# Revit family: TRP2
name_source: partatom
category: Lighting Fixtures
revit_build: Autodesk Revit 2014 (Build: 20130308_1515(x64)
units: mm (PartAtom-declared; Revit-internal decimal feet)

## types (1)
- TRP2
    Color Filter = 16777215
    Default Elevation = 48"
    Description = Mid sized architectural wallpacks in three stylish shapes with molded contours to accentuate building architecture. Provides excellent illumination in energy-saving LED systems.
    Dimming Lamp Color Temperature Shift = <None>
    Finish = Paint - Hubbell - Textured Camera Black
    Finish2 = White
    Lamp = One
    Manufacturer = Hubbell Lighting
    Model = TRP2
    Opal lens = Glass - Hubbell - White
    Photometric Web File = TRP2-24L-30-3K7-1.ies
    Product Documentation Link = https://hubbellcdn.com
    Product Page URL = https://www.hubbell.com
    Tilt Angle = 70.00°
    URL = https://www.hubbell.com
    Wattage Comments = 30W

## geometry (parser evidence)
native form markers: Blend x2
no freeform markers — native parametric forms only
